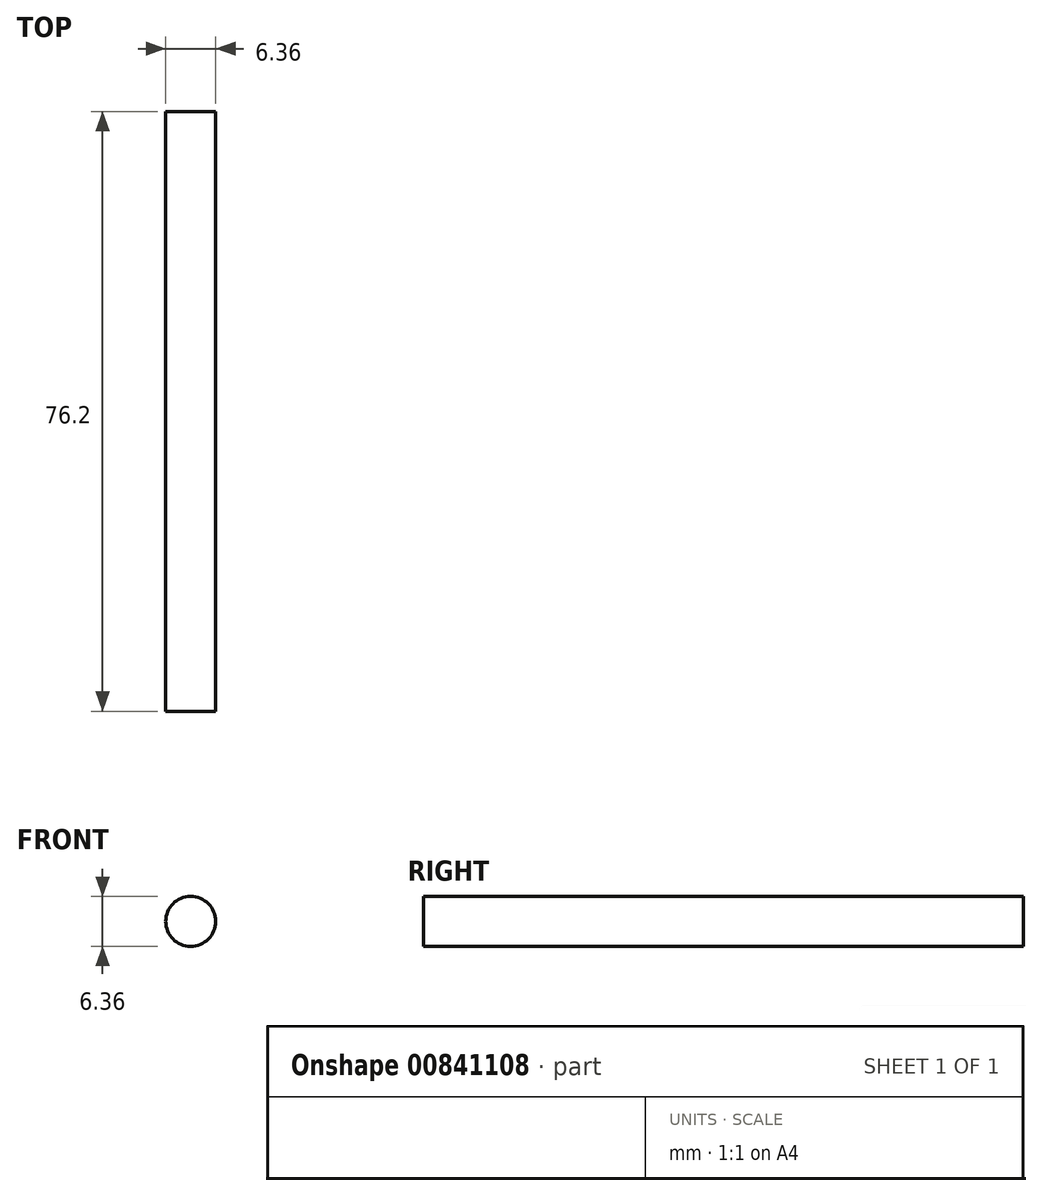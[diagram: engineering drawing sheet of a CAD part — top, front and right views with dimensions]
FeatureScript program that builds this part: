
annotation { "Feature Type Name" : "Feature", "Feature Type Description" : "" }
export const myFeature = defineFeature(function(context is Context, id is Id, definition is map)
    precondition{}
    {
        {
            var Q0;
            Q0=qCreatedBy(makeId("Front.planeOp"),FACE);
            var sketch = newSketch(context, id + "F0", { "sketchPlane" : qUnion([Q0])});
            skCircle(sketch, "E0", {"center": v(0, 0) * mm, "radius": 3.18 * mm});
            skSolve(sketch);
        }
        {
            var Q0;
            Q0 = qSketchRegion(id + "F0", true);
            extrude(context, id + "F1", {"entities" : qUnion([Q0]), "depth" : 76.2 * mm, "offsetDistance" : 25.4 * mm});
        }
    });
